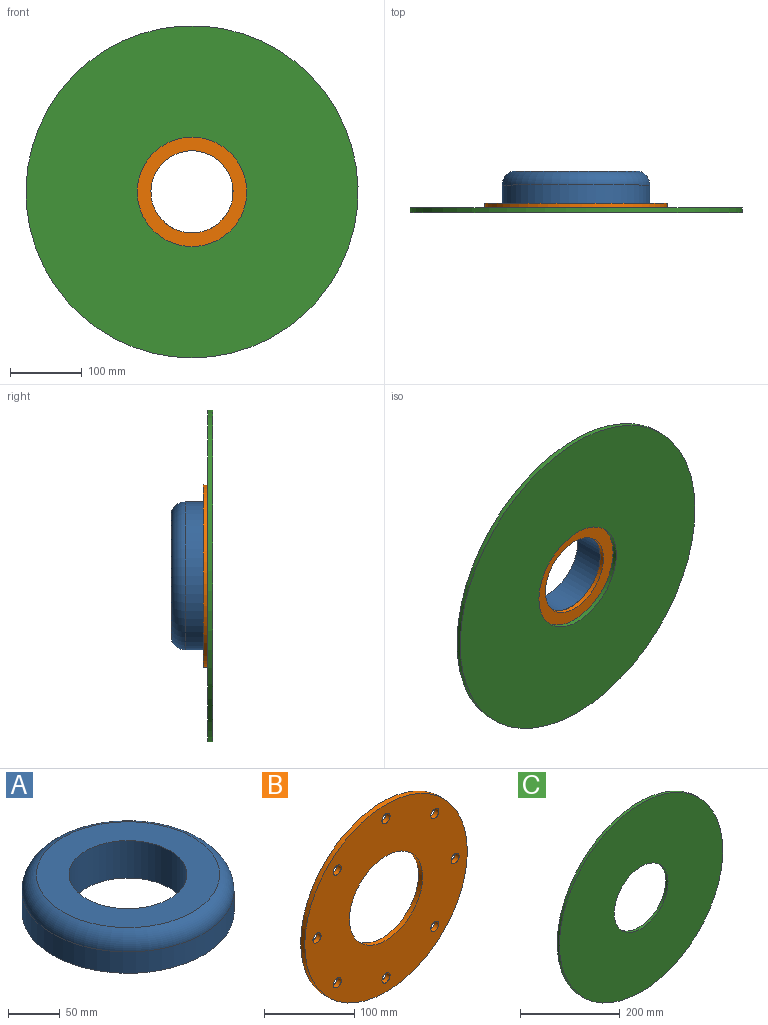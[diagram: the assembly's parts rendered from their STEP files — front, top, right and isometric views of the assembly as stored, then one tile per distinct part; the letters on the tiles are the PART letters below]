
ASSEMBLY  parts=3 mates=4
PART A: 5 faces, bbox 222.7x222.7x45.4 mm
  f0: cylinder r=102.87mm len=205.74mm, axis (0,0,-1), area 16417.3mm2, adj f1,f4
  f1: plane 205.74x205.74mm, normal (0,0,-1), area 22984.3mm2, adj f0,f2
  f2: cylinder r=57.15mm len=114.3mm, axis (0,0,-1), area 15961.3mm2, adj f1,f3
  f3: plane 177.8x177.8mm, normal (0,0,1), area 14567.8mm2, adj f2,f4
  f4: torus R=82.9mm, axis (0,0,-1), area 15556.1mm2, adj f0,f3
PART B: 12 faces, bbox 254x6.4x254 mm
  f0: cylinder r=6.35mm len=12.7mm, axis (0,1,0), area 253.4mm2, adj f10,f11
  f1: cylinder r=6.35mm len=12.7mm, axis (0,1,0), area 253.4mm2, adj f10,f11
  f2: cylinder r=6.35mm len=12.7mm, axis (0,1,0), area 253.4mm2, adj f10,f11
  f3: cylinder r=6.35mm len=12.7mm, axis (0,1,0), area 253.4mm2, adj f10,f11
  f4: cylinder r=6.35mm len=12.7mm, axis (0,1,0), area 253.4mm2, adj f10,f11
  f5: cylinder r=6.35mm len=12.7mm, axis (0,1,0), area 253.4mm2, adj f10,f11
  f6: cylinder r=6.35mm len=12.7mm, axis (0,1,0), area 253.4mm2, adj f10,f11
  f7: cylinder r=6.35mm len=12.7mm, axis (0,1,0), area 253.4mm2, adj f10,f11
  f8: cylinder r=57.15mm len=114.3mm, axis (0,1,0), area 2280.2mm2, adj f10,f11
  f9: cylinder r=127mm len=254mm, axis (0,1,0), area 5067.1mm2, adj f10,f11
  f10: plane 254x254mm, normal (0,-1,0), area 39396.5mm2, adj f0,f1,f2,f3,f4,f5,f6,f7
  f11: plane 254x254mm, normal (0,1,0), area 39396.5mm2, adj f0,f1,f2,f3,f4,f5,f6,f7
PART C: 4 faces, bbox 462.3x6.4x462.3 mm
  f0: cylinder r=76.2mm len=152.4mm, axis (0,1,0), area 3040.2mm2, adj f2,f3
  f1: cylinder r=231.14mm len=462.28mm, axis (0,1,0), area 9222.1mm2, adj f2,f3
  f2: plane 462.28x462.28mm, normal (0,-1,0), area 149600.3mm2, adj f0,f1
  f3: plane 462.28x462.28mm, normal (0,1,0), area 149600.3mm2, adj f0,f1
PLACE A rot(axis=(-1,0,0),90deg) t=(-443.23,19.05,289.49)mm
PLACE B t=(-386.08,19.05,289.49)mm
PLACE C t=(-440.64,12.7,295.5)mm
MATE cylindrical B.f8 <-> C.f0  axis (0,1,0) through (-386.08,15.87,289.49)mm
MATE planar A.f0 <-> B.f5  axis (0,-1,0) through (-386.08,19.05,289.49)mm
MATE planar C.f0 <-> B.f9  axis (0,1,0) through (-386.08,12.7,289.49)mm
MATE cylindrical A.f0 <-> B.f8  axis (0,-1,0) through (-386.08,41.27,289.49)mm
